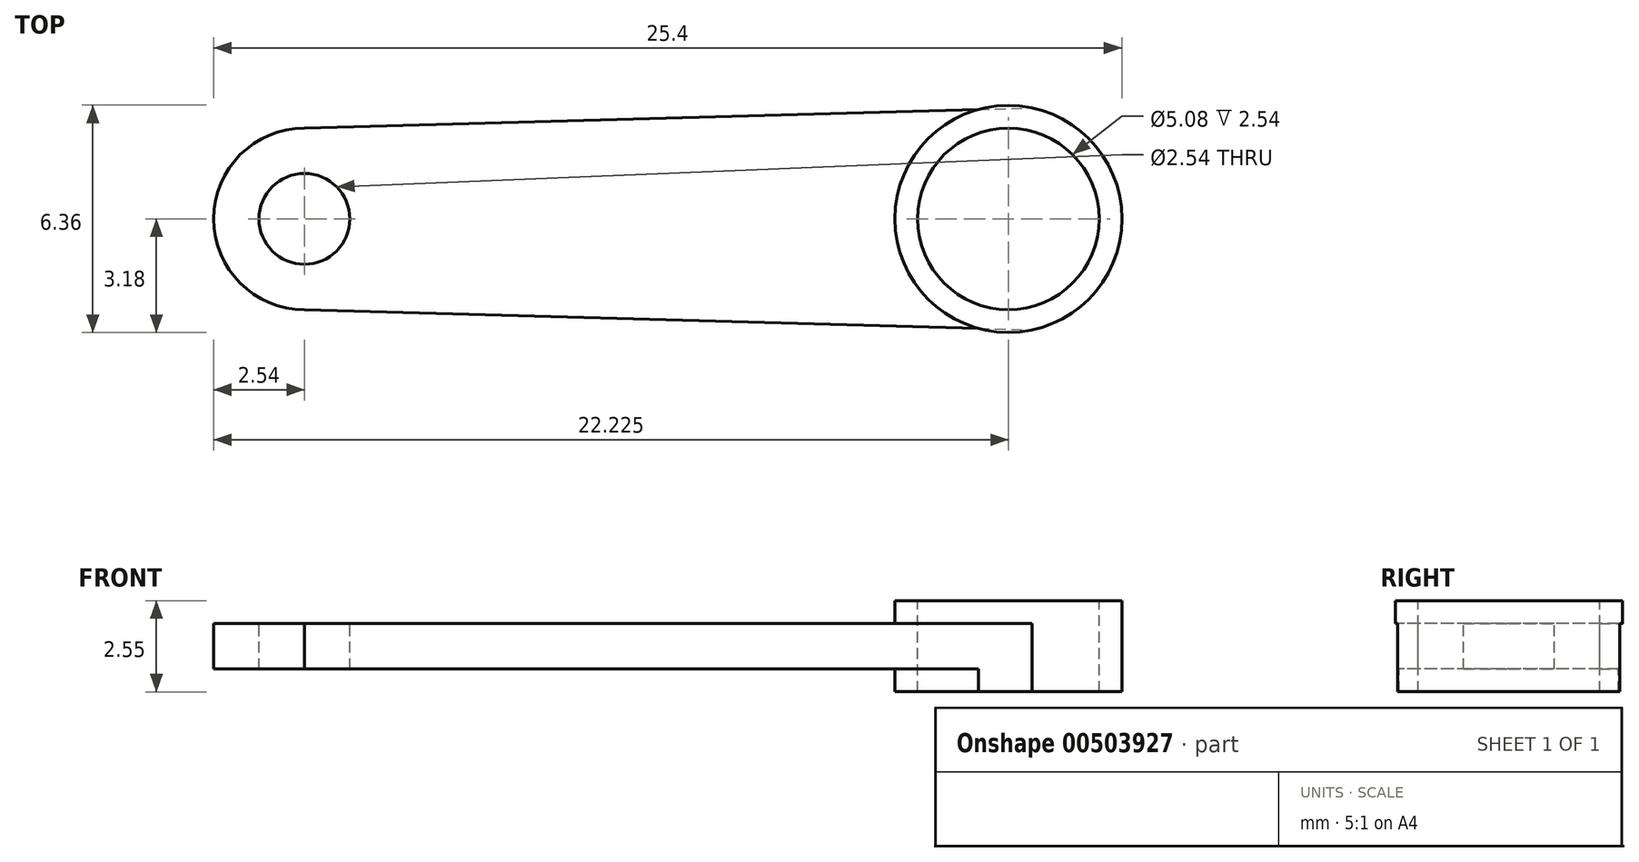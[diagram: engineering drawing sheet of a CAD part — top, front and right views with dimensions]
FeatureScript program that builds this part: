
annotation { "Feature Type Name" : "Feature", "Feature Type Description" : "" }
export const myFeature = defineFeature(function(context is Context, id is Id, definition is map)
    precondition{}
    {
        {
            var Q0;
            Q0=qCreatedBy(makeId("Top.planeOp"),FACE);
            var sketch = newSketch(context, id + "F0", { "sketchPlane" : qUnion([Q0])});
            skLineSegment(sketch, "E0.bottom", {"start": v(12.7, 3.18) * mm, "end": v(-12.7, 3.18) * mm});
            skLineSegment(sketch, "E0.top", {"start": v(12.7, -3.18) * mm, "end": v(-12.7, -3.18) * mm});
            skLineSegment(sketch, "E0.left", {"start": v(12.7, 3.18) * mm, "end": v(12.7, -3.18) * mm});
            skLineSegment(sketch, "E0.right", {"start": v(-12.7, 3.18) * mm, "end": v(-12.7, -3.18) * mm});
            skPoint(sketch, "E0.middle", {"position": v(0, 0) * mm});
            skSolve(sketch);
        }
        {
            var Q0;
            Q0=makeQuery(id+"F0.imprint","IMPRINT",FACE,{"disambiguationData":[TD([[makeQuery(id+"F0.imprint","IMPRINT",EDGE,{"derivedFrom":sQuery(id+"F0.wireOp",EDGE,"E0.bottom")}),1.0]])]});
            extrude(context, id + "F1", {"entities" : qUnion([Q0]), "depth" : 1.27 * mm});
        }
        {
            var Q0;
            Q0=makeQuery(id+"F1.opExtrude","CAP_FACE",FACE,{"disambiguationData":[OSD([sQuery(id+"F0.wireOp",EDGE,"E0.bottom"),sQuery(id+"F0.wireOp",EDGE,"E0.top"),sQuery(id+"F0.wireOp",EDGE,"E0.left"),sQuery(id+"F0.wireOp",EDGE,"E0.right")])],"isStart":false});
            var sketch = newSketch(context, id + "F2", { "sketchPlane" : qUnion([Q0])});
            skCircle(sketch, "E1", {"center": v(-10.16, 0) * mm, "radius": 2.54 * mm});
            skCircle(sketch, "E2", {"center": v(-10.16, 0) * mm, "radius": 1.27 * mm});
            skLineSegment(sketch, "E3", {"start": v(-10.16, 2.54) * mm, "end": v(12.7, 3.18) * mm});
            skLineSegment(sketch, "E4", {"start": v(-10.16, 0) * mm, "end": v(-10.16, 2.54) * mm});
            skLineSegment(sketch, "E5", {"start": v(-10.16, 0) * mm, "end": v(-10.16, -2.54) * mm});
            skLineSegment(sketch, "E6", {"start": v(-10.16, -2.54) * mm, "end": v(12.7, -3.18) * mm});
            skSolve(sketch);
        }
        {
            var Q0;
            Q0=makeQuery(id+"F1.opExtrude","CAP_FACE",FACE,{"disambiguationData":[OSD([sQuery(id+"F0.wireOp",EDGE,"E0.bottom"),sQuery(id+"F0.wireOp",EDGE,"E0.top"),sQuery(id+"F0.wireOp",EDGE,"E0.left"),sQuery(id+"F0.wireOp",EDGE,"E0.right")])],"isStart":false});
            var sketch = newSketch(context, id + "F3", { "sketchPlane" : qUnion([Q0])});
            skCircle(sketch, "E7", {"center": v(9.52, 0) * mm, "radius": 3.18 * mm});
            skSolve(sketch);
        }
        {
            var Q0;
            {var subQ0=sQuery(id+"F3.wireOp",EDGE,"E7");var subQ1=makeQuery(id+"F1.opExtrude","CAP_EDGE",EDGE,{"disambiguationData":[OSD([sQuery(id+"F0.wireOp",EDGE,"E0.left")])],"isStart":false});var subQ2=makeQuery(id+"F3.imprint","INTERSECT",VERTEX,{"derivedFrom":[subQ1,subQ0]});Q0=makeQuery(id+"F3.imprint","IMPRINT",FACE,{"disambiguationData":[TD([[makeQuery(id+"F3.imprint","IMPRINT",EDGE,{"disambiguationData":[TD([[subQ2,1.0]])],"derivedFrom":subQ0}),-1.0]])]});}
            var Q1;
            {var subQ0=sQuery(id+"F3.wireOp",EDGE,"E7");var subQ1=makeQuery(id+"F1.opExtrude","CAP_EDGE",EDGE,{"disambiguationData":[OSD([sQuery(id+"F0.wireOp",EDGE,"E0.bottom")])],"isStart":false});var subQ2=makeQuery(id+"F3.imprint","INTERSECT",VERTEX,{"derivedFrom":[subQ1,subQ0]});Q1=makeQuery(id+"F3.imprint","IMPRINT",FACE,{"disambiguationData":[TD([[makeQuery(id+"F3.imprint","IMPRINT",EDGE,{"disambiguationData":[TD([[subQ2,1.0]])],"derivedFrom":subQ0}),-1.0]])]});}
            extrude(context, id + "F4", {"entities" : qUnion([Q0, Q1]), "operationType" : NewBodyOperationType.REMOVE, "oppositeDirection" : true, "depth" : 25.4 * mm});
        }
        {
            var Q0;
            Q0=makeQuery(id+"F1.opExtrude","CAP_FACE",FACE,{"disambiguationData":[OSD([sQuery(id+"F0.wireOp",EDGE,"E0.bottom"),sQuery(id+"F0.wireOp",EDGE,"E0.top"),sQuery(id+"F0.wireOp",EDGE,"E0.left"),sQuery(id+"F0.wireOp",EDGE,"E0.right")])],"isStart":false});
            var sketch = newSketch(context, id + "F5", { "sketchPlane" : qUnion([Q0])});
            skCircle(sketch, "E8", {"center": v(9.52, 0) * mm, "radius": 3.18 * mm});
            skSolve(sketch);
        }
        {
            var Q0;
            {var subQ0=sQuery(id+"F5.wireOp",EDGE,"E8");var subQ1=makeQuery(id+"F5.imprint","INTERSECT",VERTEX,{"derivedFrom":[makeQuery(id+"F1.opExtrude","CAP_EDGE",EDGE,{"disambiguationData":[OSD([sQuery(id+"F0.wireOp",EDGE,"E0.bottom")])],"isStart":false}),subQ0]});Q0=makeQuery(id+"F5.imprint","IMPRINT",FACE,{"disambiguationData":[TD([[makeQuery(id+"F5.imprint","IMPRINT",EDGE,{"disambiguationData":[TD([[subQ1,-1.0]])],"derivedFrom":subQ0}),1.0]])]});}
            extrude(context, id + "F6", {"entities" : qUnion([Q0]), "operationType" : NewBodyOperationType.ADD, "depth" : 0.64 * mm, "hasSecondDirection" : true, "secondDirectionOppositeDirection" : true, "secondDirectionDepth" : 1.9 * mm});
        }
        {
            var Q0;
            Q0=makeQuery(id+"F6.opExtrude","CAP_FACE",FACE,{"disambiguationData":[OSD([sQuery(id+"F5.wireOp",EDGE,"E8")])],"isStart":false});
            var sketch = newSketch(context, id + "F7", { "sketchPlane" : qUnion([Q0])});
            skCircle(sketch, "E9", {"center": v(9.52, 0) * mm, "radius": 2.54 * mm});
            skSolve(sketch);
        }
        {
            var Q0;
            Q0=makeQuery(id+"F7.imprint","IMPRINT",FACE,{"disambiguationData":[TD([[makeQuery(id+"F7.imprint","IMPRINT",EDGE,{"derivedFrom":sQuery(id+"F7.wireOp",EDGE,"E9")}),1.0]])]});
            extrude(context, id + "F8", {"entities" : qUnion([Q0]), "operationType" : NewBodyOperationType.REMOVE, "oppositeDirection" : true, "depth" : 25.4 * mm});
        }
        {
            var Q0;
            {var subQ0=sQuery(id+"F2.wireOp",EDGE,"E6");Q0=makeQuery(id+"F2.imprint","IMPRINT",FACE,{"disambiguationData":[TD([[makeQuery(id+"F2.imprint","IMPRINT",EDGE,{"derivedFrom":subQ0}),-1.0]])]});}
            var Q1;
            {var subQ0=sQuery(id+"F2.wireOp",EDGE,"E3");Q1=makeQuery(id+"F2.imprint","IMPRINT",FACE,{"disambiguationData":[TD([[makeQuery(id+"F2.imprint","IMPRINT",EDGE,{"derivedFrom":subQ0}),1.0]])]});}
            var Q2;
            {var subQ0=sQuery(id+"F2.wireOp",EDGE,"E4");var subQ1=sQuery(id+"F2.wireOp",EDGE,"E2");var subQ2=makeQuery(id+"F2.imprint","INTERSECT",VERTEX,{"derivedFrom":[subQ1,subQ0]});Q2=makeQuery(id+"F2.imprint","IMPRINT",FACE,{"disambiguationData":[TD([[makeQuery(id+"F2.imprint","IMPRINT",EDGE,{"disambiguationData":[TD([[subQ2,1.0]])],"derivedFrom":subQ1}),1.0]])]});}
            var Q3;
            {var subQ0=sQuery(id+"F2.wireOp",EDGE,"E4");var subQ1=sQuery(id+"F2.wireOp",EDGE,"E2");var subQ2=makeQuery(id+"F2.imprint","INTERSECT",VERTEX,{"derivedFrom":[subQ1,subQ0]});Q3=makeQuery(id+"F2.imprint","IMPRINT",FACE,{"disambiguationData":[TD([[makeQuery(id+"F2.imprint","IMPRINT",EDGE,{"disambiguationData":[TD([[subQ2,-1.0]])],"derivedFrom":subQ1}),1.0]])]});}
            extrude(context, id + "F9", {"entities" : qUnion([Q0, Q1, Q2, Q3]), "operationType" : NewBodyOperationType.REMOVE, "oppositeDirection" : true, "depth" : 25.4 * mm});
        }
    });
